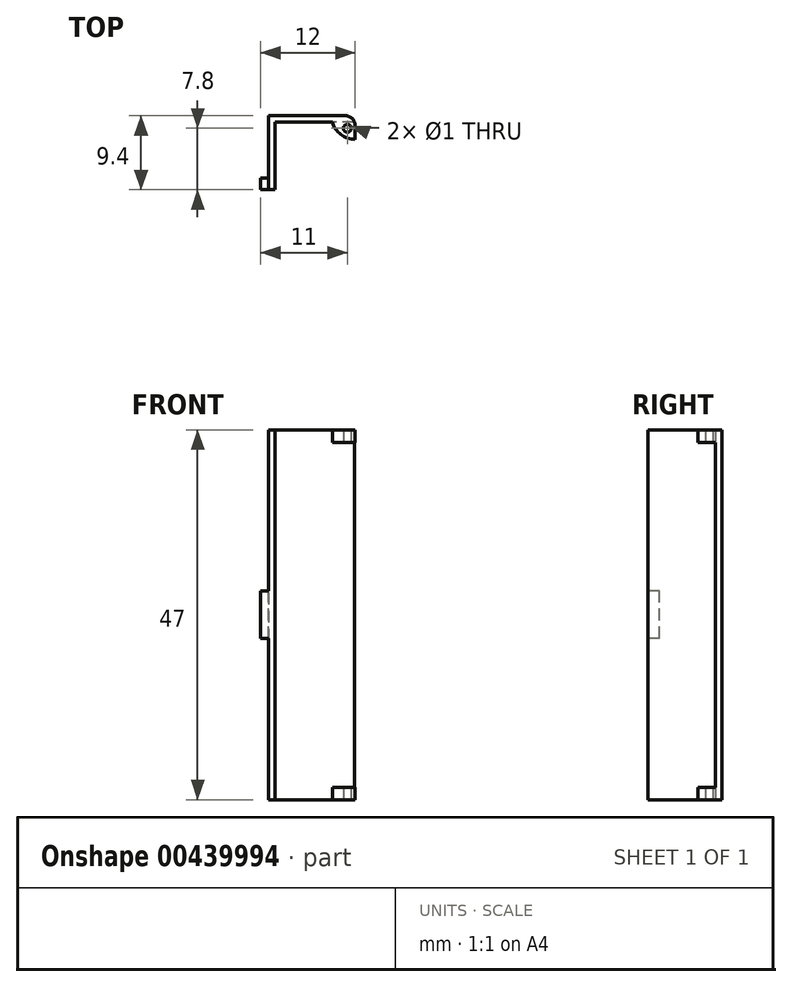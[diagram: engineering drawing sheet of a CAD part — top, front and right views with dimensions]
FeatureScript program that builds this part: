
annotation { "Feature Type Name" : "Feature", "Feature Type Description" : "" }
export const myFeature = defineFeature(function(context is Context, id is Id, definition is map)
    precondition{}
    {
        {
            var Q0;
            Q0=qCreatedBy(makeId("Top.planeOp"),FACE);
            var sketch = newSketch(context, id + "F0", { "sketchPlane" : qUnion([Q0])});
            skLineSegment(sketch, "E0.bottom", {"start": v(0, 0) * mm, "end": v(-11, 0) * mm});
            skLineSegment(sketch, "E0.top", {"start": v(-1.25, 9.4) * mm, "end": v(-11, 9.4) * mm});
            skLineSegment(sketch, "E0.left", {"start": v(0, 0) * mm, "end": v(0, 8.15) * mm});
            skLineSegment(sketch, "E0.right", {"start": v(-11, 0) * mm, "end": v(-11, 9.4) * mm});
            skLineSegment(sketch, "E1", {"start": v(-10.2, 9.4) * mm, "end": v(-10.2, 0) * mm});
            skLineSegment(sketch, "E2", {"start": v(-10.2, 8.6) * mm, "end": v(0, 8.6) * mm});
            skPoint(sketch, "E3.visualSharp", {"position": v(0, 9.4) * mm});
            skArc(sketch, "E3.filletArc", {"start": v(0, 8.15) * mm, "mid": v(-0.37, 9.03) * mm, "end": v(-1.25, 9.4) * mm});
            skPoint(sketch, "E4", {"position": v(-1, 7.8) * mm});
            skArc(sketch, "E5", {"start": v(-2.9, 8.6) * mm, "mid": v(-1.82, 7.01) * mm, "end": v(0, 6.4) * mm});
            skSolve(sketch);
        }
        {
            var Q0;
            {var subQ3=sQuery(id+"F0.wireOp",EDGE,"E5");Q0=makeQuery(id+"F0.imprint","IMPRINT",FACE,{"disambiguationData":[TD([[makeQuery(id+"F0.imprint","IMPRINT",EDGE,{"derivedFrom":subQ3}),1.0]])]});}
            var Q1;
            {var subQ2=sQuery(id+"F0.wireOp",EDGE,"E3.filletArc");var subQ6=sQuery(id+"F0.wireOp",EDGE,"E0.top");var subQ8=makeQuery(id+"F0.imprint","INTERSECT",VERTEX,{"derivedFrom":[subQ6,subQ2]});Q1=makeQuery(id+"F0.imprint","IMPRINT",FACE,{"disambiguationData":[TD([[makeQuery(id+"F0.imprint","IMPRINT",EDGE,{"disambiguationData":[TD([[subQ8,-1.0]])],"derivedFrom":subQ6}),1.0]])]});}
            var Q2;
            {var subQ4=sQuery(id+"F0.wireOp",EDGE,"E0.right");Q2=makeQuery(id+"F0.imprint","IMPRINT",FACE,{"disambiguationData":[TD([[makeQuery(id+"F0.imprint","IMPRINT",EDGE,{"derivedFrom":subQ4}),-1.0]])]});}
            extrude(context, id + "F1", {"entities" : qUnion([Q0, Q1, Q2]), "depth" : 47 * mm});
        }
        {
            var Q0;
            Q0=makeQuery(id+"F1.opExtrude","SWEPT_FACE",FACE,{"disambiguationData":[OSD([sQuery(id+"F0.wireOp",EDGE,"E1")])]});
            var sketch = newSketch(context, id + "F2", { "sketchPlane" : qUnion([Q0])});
            skLineSegment(sketch, "E6.0", {"start": v(8.6, 0) * mm, "end": v(0, 0) * mm});
            skLineSegment(sketch, "E6.1", {"start": v(8.6, 47) * mm, "end": v(0, 47) * mm});
            skLineSegment(sketch, "E6.2", {"start": v(0, 47) * mm, "end": v(0, 0) * mm});
            skLineSegment(sketch, "E7.0", {"start": v(8.6, 47) * mm, "end": v(8.6, 0) * mm});
            skLineSegment(sketch, "E8", {"start": v(8.6, 45.4) * mm, "end": v(0, 45.4) * mm});
            skLineSegment(sketch, "E9", {"start": v(8.6, 1.6) * mm, "end": v(0, 1.6) * mm});
            skSolve(sketch);
        }
        {
            var Q0;
            {var subQ0=sQuery(id+"F2.wireOp",EDGE,"E8");Q0=makeQuery(id+"F2.imprint","IMPRINT",FACE,{"disambiguationData":[TD([[makeQuery(id+"F2.imprint","IMPRINT",EDGE,{"derivedFrom":subQ0}),1.0]])]});}
            extrude(context, id + "F3", {"entities" : qUnion([Q0]), "operationType" : NewBodyOperationType.REMOVE, "depth" : 25 * mm});
        }
        {
            var Q0;
            Q0=sQuery(id+"F0.wireOp",VERTEX,"E4");
            var Q1;
            Q1=makeQuery(id+"F1.opExtrude","SWEPT_BODY",BODY,{"disambiguationData":[OSD([sQuery(id+"F0.wireOp",EDGE,"E0.bottom"),sQuery(id+"F0.wireOp",EDGE,"E0.top"),sQuery(id+"F0.wireOp",EDGE,"E0.left"),sQuery(id+"F0.wireOp",EDGE,"E0.right"),sQuery(id+"F0.wireOp",EDGE,"E1"),sQuery(id+"F0.wireOp",EDGE,"E2"),sQuery(id+"F0.wireOp",EDGE,"E3.filletArc"),sQuery(id+"F0.wireOp",EDGE,"E5")])]});
            hole(context, id + "F4", {"style" : HoleStyle.SIMPLE, "endStyle" : HoleEndStyle.THROUGH, "oppositeDirection" : true, "holeDiameter" : 1 * mm, "isTappedThrough" : true, "tappedDepth" : 12 * mm, "tapClearance" : 3, "startFromSketch" : true, "locations" : qUnion([Q0]), "scope" : qUnion([Q1])});
        }
        {
            var Q0;
            Q0=makeQuery(id+"F1.opExtrude","SWEPT_FACE",FACE,{"disambiguationData":[OSD([sQuery(id+"F0.wireOp",EDGE,"E0.right")])]});
            var sketch = newSketch(context, id + "F5", { "sketchPlane" : qUnion([Q0])});
            skLineSegment(sketch, "E10.0", {"start": v(0, 47) * mm, "end": v(0, 0) * mm});
            skPoint(sketch, "E11", {"position": v(0, 23.5) * mm});
            skPoint(sketch, "E12", {"position": v(0, 20.5) * mm});
            skPoint(sketch, "E13", {"position": v(0, 26.5) * mm});
            skPoint(sketch, "E14", {"position": v(-1.5, 20.5) * mm});
            skPoint(sketch, "E15", {"position": v(-1.5, 26.5) * mm});
            skLineSegment(sketch, "E16", {"start": v(-1.5, 20.5) * mm, "end": v(0, 20.5) * mm});
            skLineSegment(sketch, "E17", {"start": v(-1.5, 20.5) * mm, "end": v(-1.5, 26.5) * mm});
            skLineSegment(sketch, "E18", {"start": v(-1.5, 26.5) * mm, "end": v(0, 26.5) * mm});
            skSolve(sketch);
        }
        {
            var Q0;
            {var subQ0=sQuery(id+"F5.wireOp",EDGE,"E16");Q0=makeQuery(id+"F5.imprint","IMPRINT",FACE,{"disambiguationData":[TD([[makeQuery(id+"F5.imprint","IMPRINT",EDGE,{"derivedFrom":subQ0}),1.0]])]});}
            extrude(context, id + "F6", {"entities" : qUnion([Q0]), "operationType" : NewBodyOperationType.ADD, "depth" : 1 * mm});
        }
    });
